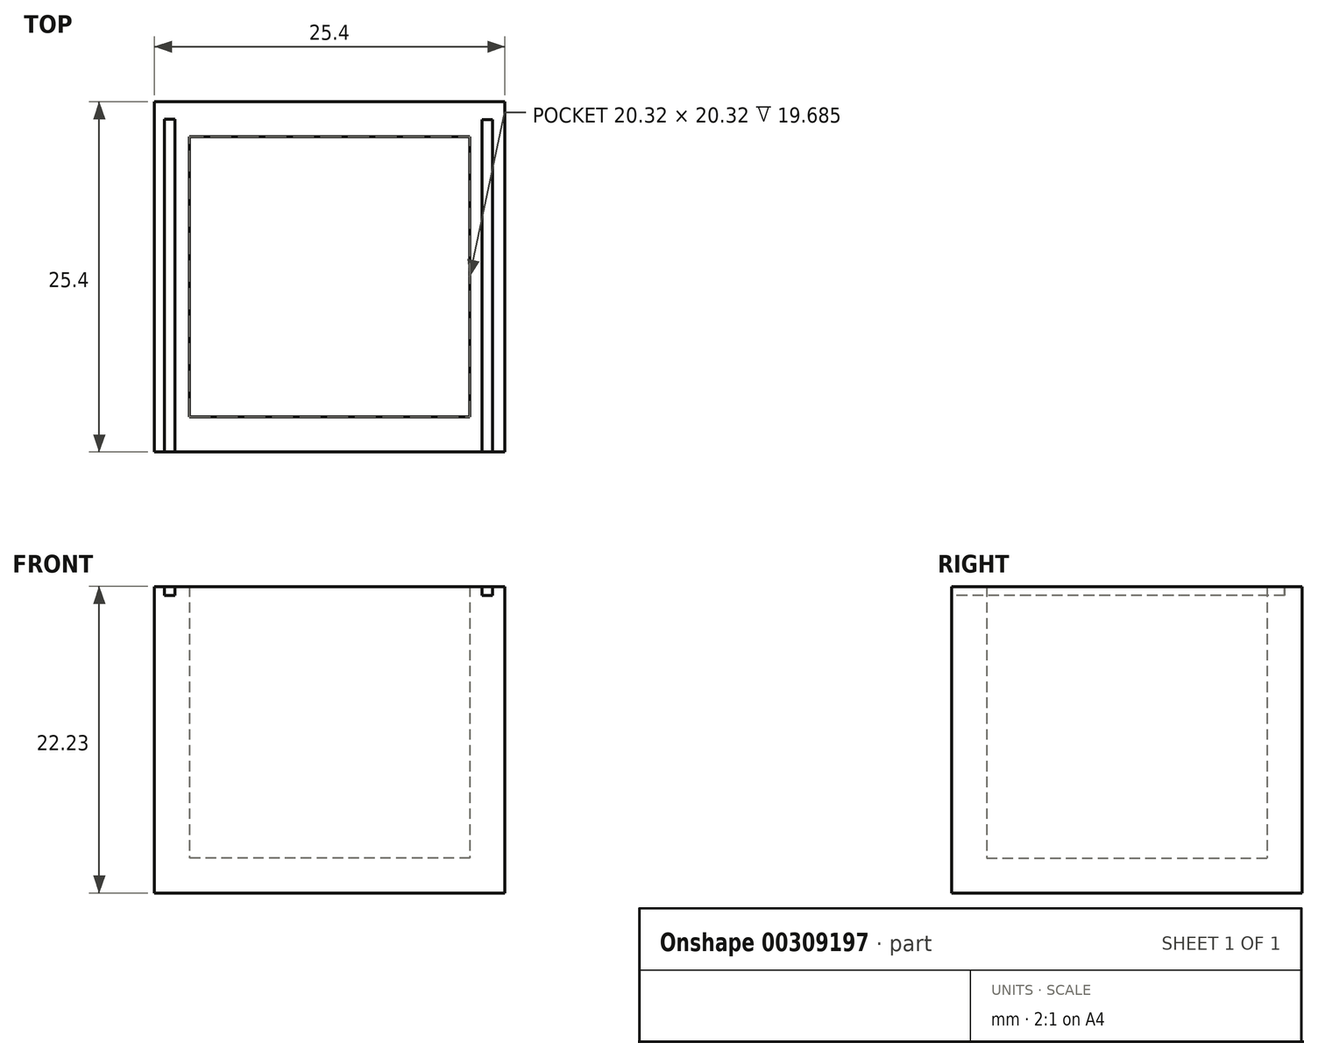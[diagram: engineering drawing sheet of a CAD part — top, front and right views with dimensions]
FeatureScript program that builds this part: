
annotation { "Feature Type Name" : "Feature", "Feature Type Description" : "" }
export const myFeature = defineFeature(function(context is Context, id is Id, definition is map)
    precondition{}
    {
        {
            var Q0;
            Q0=qCreatedBy(makeId("Top.planeOp"),FACE);
            var sketch = newSketch(context, id + "F0", { "sketchPlane" : qUnion([Q0])});
            skLineSegment(sketch, "E0.bottom", {"start": v(12.7, -12.7) * mm, "end": v(-12.7, -12.7) * mm});
            skLineSegment(sketch, "E0.top", {"start": v(12.7, 12.7) * mm, "end": v(-12.7, 12.7) * mm});
            skLineSegment(sketch, "E0.left", {"start": v(12.7, -12.7) * mm, "end": v(12.7, 12.7) * mm});
            skLineSegment(sketch, "E0.right", {"start": v(-12.7, -12.7) * mm, "end": v(-12.7, 12.7) * mm});
            skPoint(sketch, "E0.middle", {"position": v(0, 0) * mm});
            skLineSegment(sketch, "E1.bottom", {"start": v(10.16, -10.16) * mm, "end": v(-10.16, -10.16) * mm});
            skLineSegment(sketch, "E1.top", {"start": v(10.16, 10.16) * mm, "end": v(-10.16, 10.16) * mm});
            skLineSegment(sketch, "E1.left", {"start": v(10.16, -10.16) * mm, "end": v(10.16, 10.16) * mm});
            skLineSegment(sketch, "E1.right", {"start": v(-10.16, -10.16) * mm, "end": v(-10.16, 10.16) * mm});
            skSolve(sketch);
        }
        {
            var Q0;
            Q0=makeQuery(id+"F0.imprint","IMPRINT",FACE,{"disambiguationData":[TD([[makeQuery(id+"F0.imprint","IMPRINT",EDGE,{"derivedFrom":sQuery(id+"F0.wireOp",EDGE,"E1.bottom")}),-1.0]])]});
            extrude(context, id + "F1", {"entities" : qUnion([Q0]), "depth" : 2.54 * mm});
        }
        {
            var Q0;
            Q0=makeQuery(id+"F0.imprint","IMPRINT",FACE,{"disambiguationData":[TD([[makeQuery(id+"F0.imprint","IMPRINT",EDGE,{"derivedFrom":sQuery(id+"F0.wireOp",EDGE,"E0.bottom")}),-1.0]])]});
            extrude(context, id + "F2", {"entities" : qUnion([Q0]), "operationType" : NewBodyOperationType.ADD, "depth" : 21.59 * mm});
        }
        {
            var Q0;
            Q0=makeQuery(id+"F2.opExtrude","CAP_FACE",FACE,{"disambiguationData":[OSD([sQuery(id+"F0.wireOp",EDGE,"E0.bottom"),sQuery(id+"F0.wireOp",EDGE,"E0.top"),sQuery(id+"F0.wireOp",EDGE,"E0.left"),sQuery(id+"F0.wireOp",EDGE,"E0.right"),sQuery(id+"F0.wireOp",EDGE,"E1.bottom"),sQuery(id+"F0.wireOp",EDGE,"E1.top"),sQuery(id+"F0.wireOp",EDGE,"E1.left"),sQuery(id+"F0.wireOp",EDGE,"E1.right")])],"isStart":false});
            var sketch = newSketch(context, id + "F3", { "sketchPlane" : qUnion([Q0])});
            skLineSegment(sketch, "E2.bottom", {"start": v(-11.23, 11.43) * mm, "end": v(-12, 11.43) * mm});
            skLineSegment(sketch, "E2.left", {"start": v(-11.23, 11.43) * mm, "end": v(-11.23, -11.43) * mm});
            skLineSegment(sketch, "E2.right", {"start": v(-12, 11.43) * mm, "end": v(-12, -11.43) * mm});
            skPoint(sketch, "E2.middle", {"position": v(-11.61, 0) * mm});
            skLineSegment(sketch, "E3.bottom", {"start": v(11.8, 11.4) * mm, "end": v(11.03, 11.4) * mm});
            skLineSegment(sketch, "E3.left", {"start": v(11.8, 11.4) * mm, "end": v(11.8, -11.45) * mm});
            skLineSegment(sketch, "E3.right", {"start": v(11.03, 11.4) * mm, "end": v(11.03, -11.45) * mm});
            skPoint(sketch, "E3.middle", {"position": v(11.41, -0.02) * mm});
            skLineSegment(sketch, "E4", {"start": v(11.03, -11.45) * mm, "end": v(11.03, -12.7) * mm});
            skLineSegment(sketch, "E5", {"start": v(11.8, -11.45) * mm, "end": v(11.8, -12.7) * mm});
            skLineSegment(sketch, "E6", {"start": v(-12, -11.43) * mm, "end": v(-12, -12.7) * mm});
            skLineSegment(sketch, "E7", {"start": v(-11.23, -11.43) * mm, "end": v(-11.23, -12.7) * mm});
            skSolve(sketch);
        }
        {
            var Q0;
            Q0=makeQuery(id+"F3.imprint","IMPRINT",FACE,{"disambiguationData":[TD([[makeQuery(id+"F3.imprint","IMPRINT",EDGE,{"derivedFrom":sQuery(id+"F3.wireOp",EDGE,"E2.bottom")}),-1.0]])]});
            extrude(context, id + "F4", {"entities" : qUnion([Q0]), "operationType" : NewBodyOperationType.ADD, "depth" : 0.64 * mm});
        }
    });
